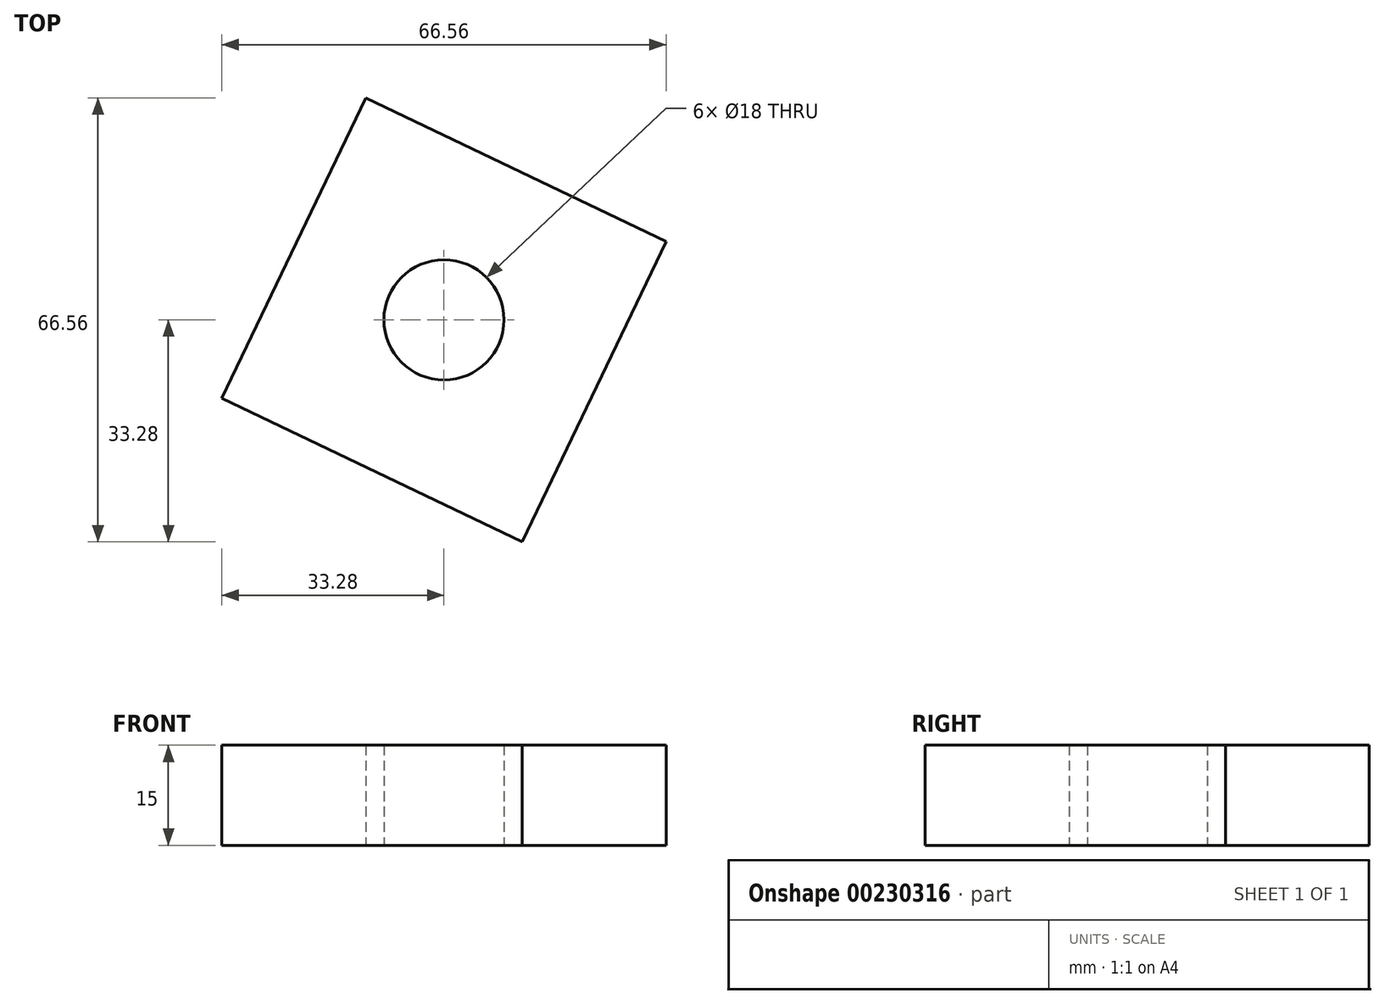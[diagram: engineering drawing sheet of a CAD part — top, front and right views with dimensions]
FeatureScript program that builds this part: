
annotation { "Feature Type Name" : "Feature", "Feature Type Description" : "" }
export const myFeature = defineFeature(function(context is Context, id is Id, definition is map)
    precondition{}
    {
        {
            var Q0;
            Q0=qCreatedBy(makeId("Top.planeOp"),FACE);
            var sketch = newSketch(context, id + "F0", { "sketchPlane" : qUnion([Q0])});
            skCircle(sketch, "E0.cCircle", {"center": v(0, 0) * mm, "radius": 24.95 * mm, "construction": true});
            skLineSegment(sketch, "E0.0", {"start": v(33.28, 11.72) * mm, "end": v(11.72, -33.28) * mm});
            skLineSegment(sketch, "E0.1", {"start": v(11.72, -33.28) * mm, "end": v(-33.28, -11.72) * mm});
            skLineSegment(sketch, "E0.2", {"start": v(-33.28, -11.72) * mm, "end": v(-11.72, 33.28) * mm});
            skLineSegment(sketch, "E0.3", {"start": v(-11.72, 33.28) * mm, "end": v(33.28, 11.72) * mm});
            skPoint(sketch, "E0.0.midPoint", {"position": v(22.5, -10.78) * mm});
            skCircle(sketch, "E1", {"center": v(0, 0) * mm, "radius": 9 * mm});
            skSolve(sketch);
        }
        {
            var Q0;
            Q0 = qSketchRegion(id + "F0", true);
            extrude(context, id + "F1", {"entities" : qUnion([Q0]), "depth" : 15 * mm});
        }
    });
